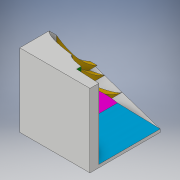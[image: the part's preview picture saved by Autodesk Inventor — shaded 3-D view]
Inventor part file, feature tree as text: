
AUTODESK INVENTOR PART (.ipt)
format: ipt  version: 2019.3 (Build 233278000, 278)  size: 283,648 bytes
history: native  units: in
note: dims shown in document units (in); Inventor stores cm internally (conversion verified against a paired STEP export)
features: plane x16, sketch x15, extrude x8
ambient origin geometry x8: Origin, YZ Plane, XZ Plane, XY Plane, X Axis, Y Axis, Z Axis, Center Point
bodies: Body1 (feature_tree)
feature tree (39):
  sketch  "Sketch1"  dims[d0=4.7244in d1=1.9685in]
  plane  "Work Plane2"
  sketch  "Sketch2"  dims[d2=0.5906in d5=0.315in]
  extrude  "Extrusion2"  Depth=1.9685in
  extrude  "Extrusion3"  Depth=0.315in
  plane  "Work Plane4"
  plane  "Work Plane5"
  sketch  "Sketch3"  dims[d7=2.7559in d12=1.5748in]
  plane  "Work Plane6"
  extrude  "Extrusion5"  Depth=1.5748in
  plane  "Work Plane7"
  sketch  "Sketch5"  dims[d17=-2.1559in d18=2.1559in d19=-1.378in]
  plane  "Work Plane8"
  extrude  "Extrusion6"  Depth=4.7244in TaperAngle=0.0deg
  sketch  "Sketch7"  dims[d24=0.1181in d25=0.0in d26=-2.3622in]
  sketch  "3D Sketch3"
  plane  "Work Plane11"
  plane  "Work Plane12"
  sketch  "Sketch12"  dims[d27=2.5591in d28=0.3937in d29=0.0in]
  plane  "Work Plane13"
  sketch  "Sketch13"  dims[d30=2.9528in]
  plane  "Work Plane14"
  plane  "Work Plane16"
  sketch  "Sketch17"  dims[d34=-2.1654in]
  plane  "Work Plane18"
  sketch  "Sketch18"  dims[d35=0.0in]
  plane  "Work Plane19"
  extrude  "Extrusion11"  [1 undecoded]
  plane  "Work Plane20"
  extrude  "Extrusion12"  Depth=2.7559in
  plane  "Work Plane21"
  extrude  "Extrusion13"  [1 undecoded]
  extrude  "Extrusion14"  Depth=0.3937in TaperAngle=0.0deg
  plane  "Work Plane3"
  sketch  "Sketch4"  dims[d13=4.7244in d14=0.0in d15=4.7244in d16=0.0in]
  sketch  "Sketch6"  dims[d20=1.378in d23=2.7559in]
  sketch  "Sketch19"  dims[d37=3.937in]
  sketch  "Sketch20"  dims[d38=3.937in]
  sketch  "Sketch21"  dims[d39=-1.75in d41=-2.1457in d46=3.3465in d47=90.0deg d52=-0.9843in d53=0.9843in d54=0.0in d55=0.4921in d56=0.0in d57=-2.1654in d58=1.5748in d59=0.0in d60=0.1969in d61=0.0in]
note: 2 required parameter values undecoded (feature->parameter linkage not recoverable at this tier; creation-order binding heuristic only, values carry confidence <= 0.55)
